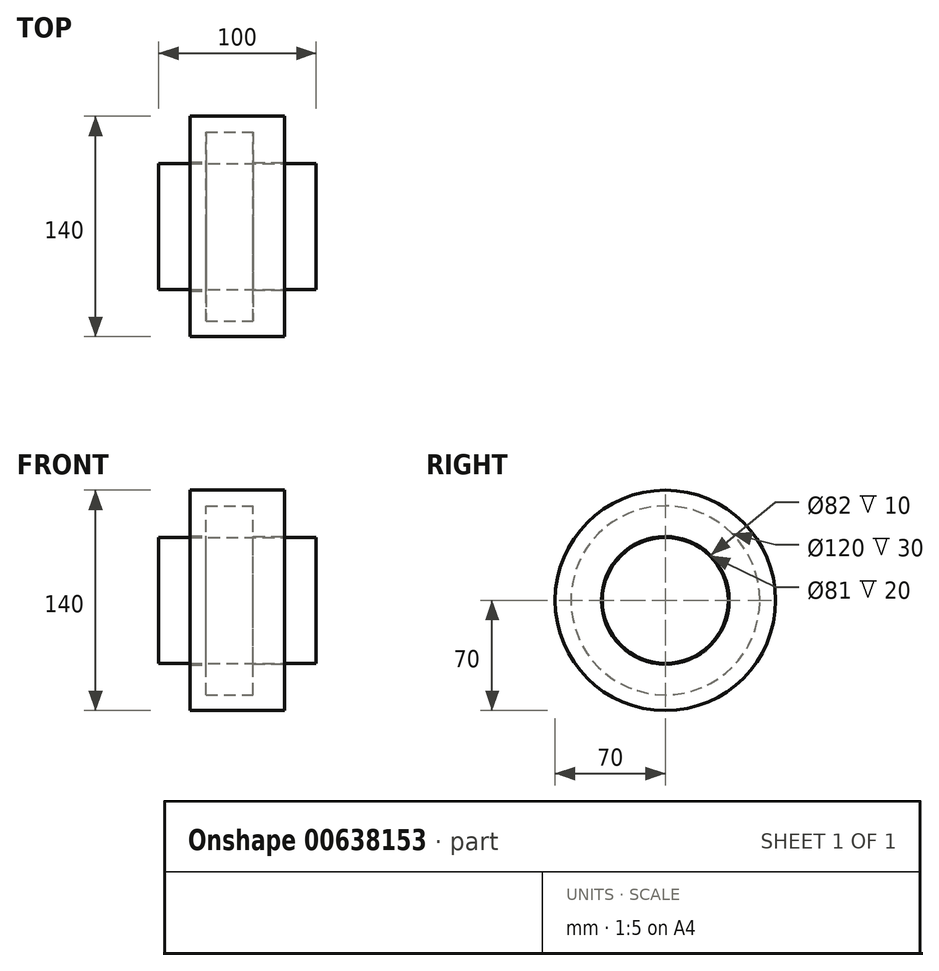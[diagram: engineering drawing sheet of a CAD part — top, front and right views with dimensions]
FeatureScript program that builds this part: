
annotation { "Feature Type Name" : "Feature", "Feature Type Description" : "" }
export const myFeature = defineFeature(function(context is Context, id is Id, definition is map)
    precondition{}
    {
        {
            var Q0;
            Q0=qCreatedBy(makeId("Front.planeOp"),FACE);
            var sketch = newSketch(context, id + "F0", { "sketchPlane" : qUnion([Q0])});
            skLineSegment(sketch, "E0.bottom", {"start": v(50, 0) * mm, "end": v(-50, 0) * mm});
            skLineSegment(sketch, "E0.top", {"start": v(50, 40) * mm, "end": v(-50, 40) * mm});
            skLineSegment(sketch, "E0.left", {"start": v(50, 0) * mm, "end": v(50, 40) * mm});
            skLineSegment(sketch, "E0.right", {"start": v(-50, 0) * mm, "end": v(-50, 40) * mm});
            skLineSegment(sketch, "E1.bottom", {"start": v(-30, 41) * mm, "end": v(-20, 41) * mm});
            skLineSegment(sketch, "E1.top", {"start": v(-30, 70) * mm, "end": v(30, 70) * mm});
            skLineSegment(sketch, "E1.left", {"start": v(-30, 41) * mm, "end": v(-30, 70) * mm});
            skLineSegment(sketch, "E1.right", {"start": v(30, 40.5) * mm, "end": v(30, 70) * mm});
            skLineSegment(sketch, "E2.top", {"start": v(-20, 60) * mm, "end": v(10, 60) * mm});
            skLineSegment(sketch, "E2.left", {"start": v(-20, 41) * mm, "end": v(-20, 60) * mm});
            skLineSegment(sketch, "E2.right", {"start": v(10, 40.5) * mm, "end": v(10, 60) * mm});
            skLineSegment(sketch, "E3.trimOffspring", {"start": v(10, 40.5) * mm, "end": v(30, 40.5) * mm});
            skLineSegment(sketch, "E4", {"start": v(0, 70) * mm, "end": v(0, 0) * mm, "construction": true});
            skLineSegment(sketch, "E5", {"start": v(-50, 0) * mm, "end": v(-84.31, 0) * mm, "construction": true});
            skSolve(sketch);
        }
        {
            var Q0;
            Q0 = qSketchRegion(id + "F0", true);
            var Q1;
            Q1=sQuery(id+"F0.wireOp",EDGE,"E5");
            revolve(context, id + "F1", {"entities" : qUnion([Q0]), "axis" : qUnion([Q1]), "revolveType" : RevolveType.FULL});
        }
    });
